# Revit family: FH1 -  400 bis 1000
name_source: partatom
category: HLS-Bauteile
revit_build: Autodesk Revit 2017 (Build: 20190507_1515(x64)
units: mm (PartAtom-declared; Revit-internal decimal feet)

## family parameters
Arbeitsebenenbasiert = Ja
Beim Laden mit Abzugskörper schneiden = Nein
Bemaßung runder Anschluss = Durchmesser verwenden
Gemeinsam genutzt = Ja
Immer vertikal = Nein
Raumberechnungspunkt = Nein
Teiletyp = Normal

## types (3) — shared parameters
Anschluss = M12
Breite = 60 mm  [stored 0.19685 ft]
Fabrikat = MEFA
Firma = MEFA Befestigungs- und Montagesysteme GmbH
Höhe = 105 mm
Länge = 50 mm  [stored 0.164042 ft]
Material = Stahl
Materialname = S235
Mengeneinheit = St
Oberflaeche = galvanisch verzinkt
Vorgabe-Ansicht = 1219 mm
min. Lastbereich = 0 N
vpe = 1 St

## per-type parameters (varying)
| type | Artikelnummer | EAN | Federrate | Gewicht | Gewicht pro Bauteil | Kurztext1 | Kurztext2 | max. Federweg | max. Lastbereich |
| Federhänger FH1 - 1000 | 0794100 | 4250928419101 | 34,43 N/mm | 0.58 kg | 0.58 kg | Federhänger FH 1 - 1000 | F 0 - 1.006 N max. Federweg 32 mm | 32 mm  [stored 0.104987 ft] | 1.006 N |
| Federhänger FH1 -  600 | 0794060 | 4250928419095 | 20,62 N/mm | 0.55 kg | 0.55 kg | Federhänger FH 1 - 600 | F 0 - 619 N max. Federweg 30 mm | 30 mm  [stored 0.0984252 ft] | 619 N |
| Federhänger FH1 -  400 | 0794040 | 4250928419088 | 12,87 N/mm | 0.59 kg | 0.59 kg | Federhänger FH 1 - 400 | F 0 - 386 N max. Federweg 30 mm | 30 mm  [stored 0.0984252 ft] | 386 N |

note: [stored X ft] marks values corroborated as IEEE doubles in the binary element streams (Revit-internal decimal feet)
